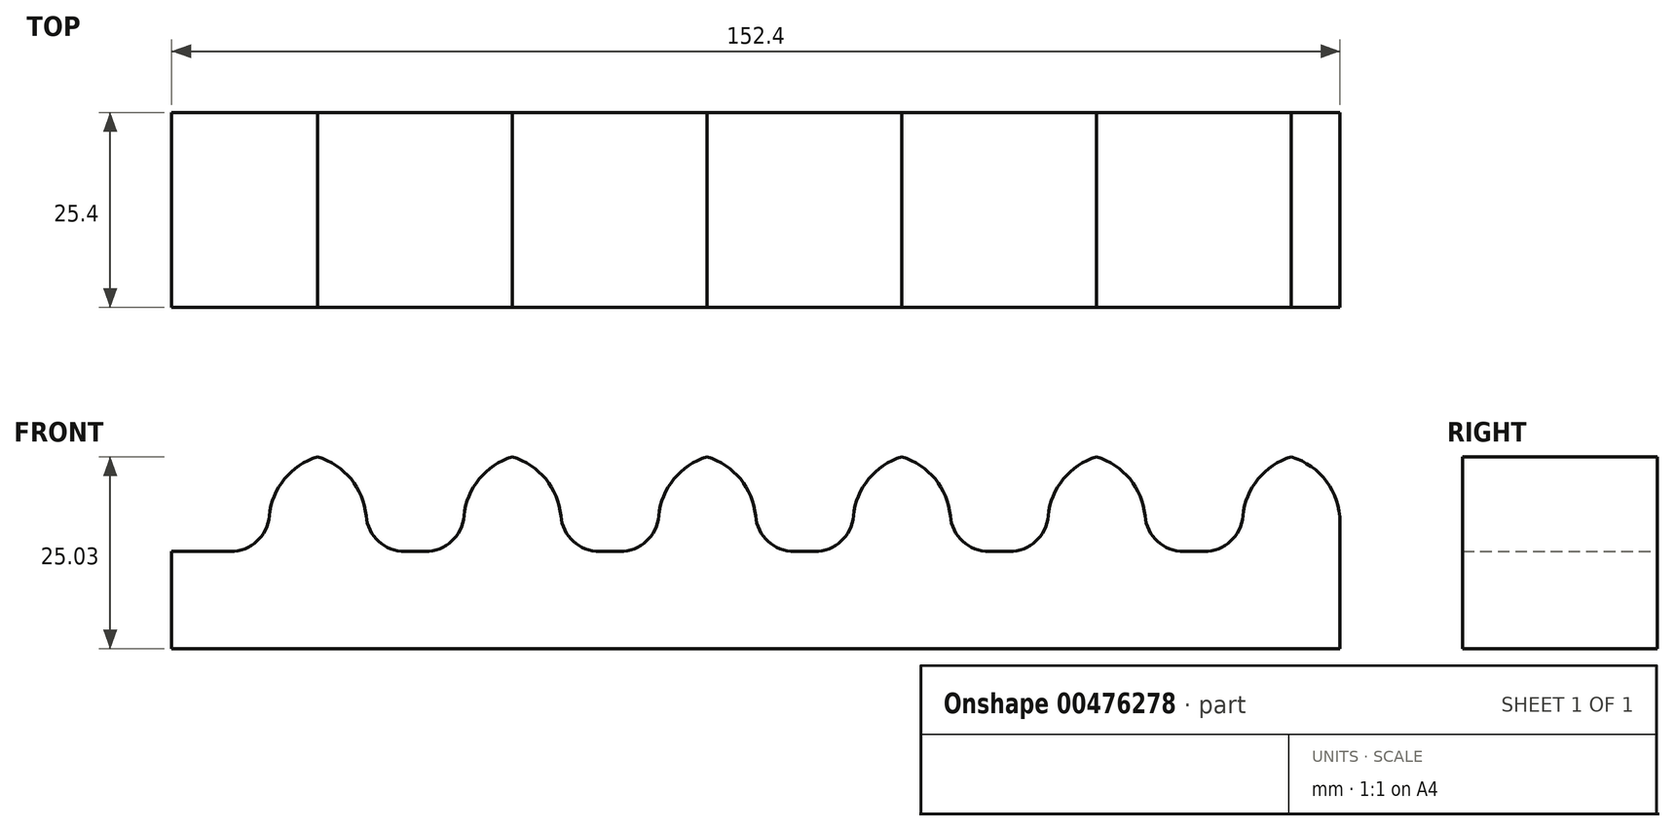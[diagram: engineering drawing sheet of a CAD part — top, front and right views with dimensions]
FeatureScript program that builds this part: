
annotation { "Feature Type Name" : "Feature", "Feature Type Description" : "" }
export const myFeature = defineFeature(function(context is Context, id is Id, definition is map)
    precondition{}
    {
        {
            var Q0;
            Q0=qCreatedBy(makeId("Front.planeOp"),FACE);
            var sketch = newSketch(context, id + "F0", { "sketchPlane" : qUnion([Q0])});
            skLineSegment(sketch, "E0.bottom", {"start": v(0, 0) * mm, "end": v(-76.2, 0) * mm});
            skLineSegment(sketch, "E0.top", {"start": v(0, -12.7) * mm, "end": v(-76.2, -12.7) * mm});
            skLineSegment(sketch, "E0.right", {"start": v(-76.2, 0) * mm, "end": v(-76.2, -12.7) * mm});
            skLineSegment(sketch, "E1.bottom", {"start": v(-76.2, 0) * mm, "end": v(76.2, 0) * mm});
            skLineSegment(sketch, "E1.top", {"start": v(-76.2, -12.7) * mm, "end": v(76.2, -12.7) * mm});
            skLineSegment(sketch, "E1.right", {"start": v(76.2, 0) * mm, "end": v(76.2, -12.7) * mm});
            skLineSegment(sketch, "E2", {"start": v(-76.2, 0) * mm, "end": v(-76.2, 12.7) * mm, "construction": true});
            skLineSegment(sketch, "E3", {"start": v(-76.2, 12.7) * mm, "end": v(76.2, 12.7) * mm, "construction": true});
            skLineSegment(sketch, "E4", {"start": v(76.2, 12.7) * mm, "end": v(76.2, 0) * mm, "construction": true});
            skLineSegment(sketch, "E5", {"start": v(63.5, 0) * mm, "end": v(63.5, 12.7) * mm});
            skLineSegment(sketch, "E6", {"start": v(63.5, 12.7) * mm, "end": v(76.2, 12.7) * mm});
            skLineSegment(sketch, "E7", {"start": v(76.2, 12.7) * mm, "end": v(76.2, 0) * mm});
            skLineSegment(sketch, "E8", {"start": v(50.8, 0) * mm, "end": v(50.8, 12.7) * mm});
            skLineSegment(sketch, "E9", {"start": v(50.8, 12.7) * mm, "end": v(38.1, 12.7) * mm});
            skLineSegment(sketch, "E10", {"start": v(38.1, 12.7) * mm, "end": v(38.1, 0) * mm});
            skLineSegment(sketch, "E11", {"start": v(25.4, 12.7) * mm, "end": v(25.4, 0) * mm});
            skLineSegment(sketch, "E12", {"start": v(25.4, 0) * mm, "end": v(12.7, 0) * mm});
            skLineSegment(sketch, "E13", {"start": v(12.7, 0) * mm, "end": v(12.7, 12.7) * mm});
            skLineSegment(sketch, "E14", {"start": v(12.7, 12.7) * mm, "end": v(25.4, 12.7) * mm});
            skLineSegment(sketch, "E15", {"start": v(0, 12.7) * mm, "end": v(0, 0) * mm});
            skLineSegment(sketch, "E16", {"start": v(0, 0) * mm, "end": v(-12.7, 0) * mm});
            skLineSegment(sketch, "E17", {"start": v(-12.7, 0) * mm, "end": v(-12.7, 12.7) * mm});
            skLineSegment(sketch, "E18", {"start": v(-12.7, 12.7) * mm, "end": v(0, 12.7) * mm});
            skLineSegment(sketch, "E19", {"start": v(-25.4, 12.7) * mm, "end": v(-25.4, 0) * mm});
            skLineSegment(sketch, "E20", {"start": v(-25.4, 0) * mm, "end": v(-38.1, 0) * mm});
            skLineSegment(sketch, "E21", {"start": v(-38.1, 0) * mm, "end": v(-38.1, 12.7) * mm});
            skLineSegment(sketch, "E22", {"start": v(-38.1, 12.7) * mm, "end": v(-25.4, 12.7) * mm});
            skLineSegment(sketch, "E23", {"start": v(-50.8, 12.7) * mm, "end": v(-50.8, 0) * mm});
            skLineSegment(sketch, "E24", {"start": v(-50.8, 0) * mm, "end": v(-63.5, 0) * mm});
            skLineSegment(sketch, "E25", {"start": v(-63.5, 0) * mm, "end": v(-63.5, 12.7) * mm});
            skLineSegment(sketch, "E26", {"start": v(-63.5, 12.7) * mm, "end": v(-50.8, 12.7) * mm});
            skSolve(sketch);
        }
        {
            var Q0;
            Q0 = qSketchRegion(id + "F0", true);
            extrude(context, id + "F1", {"entities" : qUnion([Q0]), "depth" : 25.4 * mm});
        }
        {
            var Q0;
            Q0=makeQuery(id+"F1.opExtrude","SWEPT_EDGE",EDGE,{"disambiguationData":[OSD([sQuery(id+"F0.wireOp",EDGE,"E25"),sQuery(id+"F0.wireOp",EDGE,"E26")])]});
            var Q1;
            Q1=makeQuery(id+"F1.opExtrude","SWEPT_EDGE",EDGE,{"disambiguationData":[OSD([sQuery(id+"F0.wireOp",EDGE,"E23"),sQuery(id+"F0.wireOp",EDGE,"E26")])]});
            var Q2;
            Q2=makeQuery(id+"F1.opExtrude","SWEPT_EDGE",EDGE,{"disambiguationData":[OSD([sQuery(id+"F0.wireOp",EDGE,"E21"),sQuery(id+"F0.wireOp",EDGE,"E22")])]});
            var Q3;
            Q3=makeQuery(id+"F1.opExtrude","SWEPT_EDGE",EDGE,{"disambiguationData":[OSD([sQuery(id+"F0.wireOp",EDGE,"E19"),sQuery(id+"F0.wireOp",EDGE,"E22")])]});
            var Q4;
            Q4=makeQuery(id+"F1.opExtrude","SWEPT_EDGE",EDGE,{"disambiguationData":[OSD([sQuery(id+"F0.wireOp",EDGE,"E17"),sQuery(id+"F0.wireOp",EDGE,"E18")])]});
            var Q5;
            Q5=makeQuery(id+"F1.opExtrude","SWEPT_EDGE",EDGE,{"disambiguationData":[OSD([sQuery(id+"F0.wireOp",EDGE,"E15"),sQuery(id+"F0.wireOp",EDGE,"E18")])]});
            var Q6;
            Q6=makeQuery(id+"F1.opExtrude","SWEPT_EDGE",EDGE,{"disambiguationData":[OSD([sQuery(id+"F0.wireOp",EDGE,"E13"),sQuery(id+"F0.wireOp",EDGE,"E14")])]});
            var Q7;
            Q7=makeQuery(id+"F1.opExtrude","SWEPT_EDGE",EDGE,{"disambiguationData":[OSD([sQuery(id+"F0.wireOp",EDGE,"E11"),sQuery(id+"F0.wireOp",EDGE,"E14")])]});
            var Q8;
            Q8=makeQuery(id+"F1.opExtrude","SWEPT_EDGE",EDGE,{"disambiguationData":[OSD([sQuery(id+"F0.wireOp",EDGE,"E9"),sQuery(id+"F0.wireOp",EDGE,"E10")])]});
            var Q9;
            Q9=makeQuery(id+"F1.opExtrude","SWEPT_EDGE",EDGE,{"disambiguationData":[OSD([sQuery(id+"F0.wireOp",EDGE,"E8"),sQuery(id+"F0.wireOp",EDGE,"E9")])]});
            var Q10;
            Q10=makeQuery(id+"F1.opExtrude","SWEPT_EDGE",EDGE,{"disambiguationData":[OSD([sQuery(id+"F0.wireOp",EDGE,"E6"),sQuery(id+"F0.wireOp",EDGE,"E7")])]});
            var Q11;
            Q11=makeQuery(id+"F1.opExtrude","SWEPT_EDGE",EDGE,{"disambiguationData":[OSD([sQuery(id+"F0.wireOp",EDGE,"E5"),sQuery(id+"F0.wireOp",EDGE,"E6")])]});
            fillet(context, id + "F2", {"entities" : qUnion([Q0, Q1, Q2, Q3, Q4, Q5, Q6, Q7, Q8, Q9, Q10, Q11]), "radius" : 8.9 * mm, "tangentPropagation" : true, "allowEdgeOverflow" : false});
        }
        {
            var Q0;
            Q0=makeQuery(id+"F1.opExtrude","SWEPT_EDGE",EDGE,{"disambiguationData":[OSD([sQuery(id+"F0.wireOp",EDGE,"E1.bottom"),sQuery(id+"F0.wireOp",EDGE,"E24"),sQuery(id+"F0.wireOp",EDGE,"E25")])]});
            var Q1;
            Q1=makeQuery(id+"F1.opExtrude","SWEPT_EDGE",EDGE,{"disambiguationData":[OSD([sQuery(id+"F0.wireOp",EDGE,"E1.bottom"),sQuery(id+"F0.wireOp",EDGE,"E23"),sQuery(id+"F0.wireOp",EDGE,"E24")])]});
            var Q2;
            Q2=makeQuery(id+"F1.opExtrude","SWEPT_EDGE",EDGE,{"disambiguationData":[OSD([sQuery(id+"F0.wireOp",EDGE,"E1.bottom"),sQuery(id+"F0.wireOp",EDGE,"E20"),sQuery(id+"F0.wireOp",EDGE,"E21")])]});
            var Q3;
            Q3=makeQuery(id+"F1.opExtrude","SWEPT_EDGE",EDGE,{"disambiguationData":[OSD([sQuery(id+"F0.wireOp",EDGE,"E1.bottom"),sQuery(id+"F0.wireOp",EDGE,"E19"),sQuery(id+"F0.wireOp",EDGE,"E20")])]});
            var Q4;
            Q4=makeQuery(id+"F1.opExtrude","SWEPT_EDGE",EDGE,{"disambiguationData":[OSD([sQuery(id+"F0.wireOp",EDGE,"E1.bottom"),sQuery(id+"F0.wireOp",EDGE,"E16"),sQuery(id+"F0.wireOp",EDGE,"E17")])]});
            var Q5;
            Q5=makeQuery(id+"F1.opExtrude","SWEPT_EDGE",EDGE,{"disambiguationData":[OSD([sQuery(id+"F0.wireOp",EDGE,"E1.bottom"),sQuery(id+"F0.wireOp",EDGE,"E15"),sQuery(id+"F0.wireOp",EDGE,"E16")])]});
            var Q6;
            Q6=makeQuery(id+"F1.opExtrude","SWEPT_EDGE",EDGE,{"disambiguationData":[OSD([sQuery(id+"F0.wireOp",EDGE,"E1.bottom"),sQuery(id+"F0.wireOp",EDGE,"E12"),sQuery(id+"F0.wireOp",EDGE,"E13")])]});
            var Q7;
            Q7=makeQuery(id+"F1.opExtrude","SWEPT_EDGE",EDGE,{"disambiguationData":[OSD([sQuery(id+"F0.wireOp",EDGE,"E1.bottom"),sQuery(id+"F0.wireOp",EDGE,"E10")])]});
            var Q8;
            Q8=makeQuery(id+"F1.opExtrude","SWEPT_EDGE",EDGE,{"disambiguationData":[OSD([sQuery(id+"F0.wireOp",EDGE,"E1.bottom"),sQuery(id+"F0.wireOp",EDGE,"E5")])]});
            var Q9;
            Q9=makeQuery(id+"F1.opExtrude","SWEPT_EDGE",EDGE,{"disambiguationData":[OSD([sQuery(id+"F0.wireOp",EDGE,"E1.bottom"),sQuery(id+"F0.wireOp",EDGE,"E8")])]});
            var Q10;
            Q10=makeQuery(id+"F1.opExtrude","SWEPT_EDGE",EDGE,{"disambiguationData":[OSD([sQuery(id+"F0.wireOp",EDGE,"E1.bottom"),sQuery(id+"F0.wireOp",EDGE,"E11"),sQuery(id+"F0.wireOp",EDGE,"E12")])]});
            fillet(context, id + "F3", {"entities" : qUnion([Q0, Q1, Q2, Q3, Q4, Q5, Q6, Q7, Q8, Q9, Q10]), "radius" : 5.08 * mm, "tangentPropagation" : true, "allowEdgeOverflow" : false});
        }
    });
